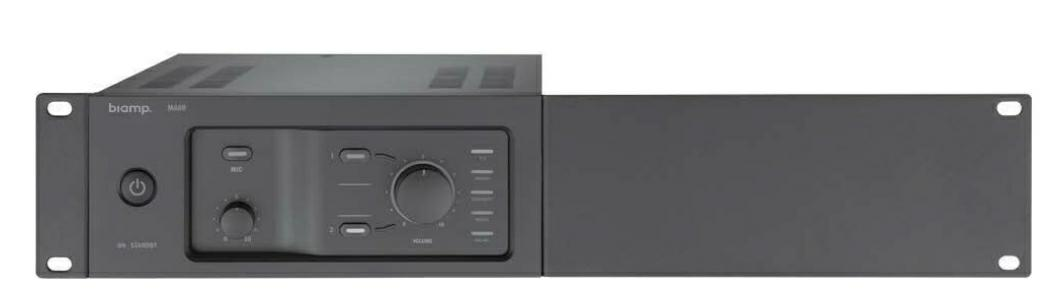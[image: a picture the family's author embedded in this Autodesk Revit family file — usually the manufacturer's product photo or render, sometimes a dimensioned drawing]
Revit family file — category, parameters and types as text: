
# Revit family: 1Electronics_Amplifier_Biamp_Commercial-Audio-Mixing-Amplifiers_MA30_MA60
name_source: partatom
category: Communication Devices
units: mm (PartAtom-declared; Revit-internal decimal feet)

## family parameters
Cut with Voids When Loaded = No
Host = Face
Maintain Annotation Orientation = No
OmniClass Number = 23.85.10.11.14
OmniClass Title = Audio Equipment
Part Type = Normal
Room Calculation Point = No
Round Connector Dimension = Use Diameter
Shared = No

## types (2) — shared parameters
Altitude = 0-6,600 ft (0-2000m) MSL
Compliance = FCC Part 15B (USA) UL listed (USA and Canada) CE Marked (Europe) RoHS Directive (Europe)
Cooling = Convection
Default Elevation = 4' - 0"
Depth = 0' - 10"
Dynamic Power = 35 W
Front Panel Indicators = Signal present, clipping, overload condition, emergency mode active, paging active, VOX active
Height = 0' - 3 1/2"
Housing Material = Biamp - Metal - Black
Humidity = 0-95% relative humidity (non-condensing)
Inputs 1-2 = -44 dBV (6 mVrms ± 10%)
Low Impedance Mode = Yes
Manufacturer = Biamp
Mic (Balanced, VOX of) = -70 dBV (0.3 mVrms ± 10%)
Mic (RCA) = -46 dBV (5 mVrms ± 10%)
Minimum Operational Load = 4Ω
No mount = No mount
Number of Output Channels = 1
Number of Poles = 1
Output Connectors = 4-pin, 0.3 inch (7.6 mm) Euroblock
Power Factor = 1
Product Documentation Link = https://downloads.biamp.com
Product Page URL = https://www.biamp.com
Product data url = https://www.bimobject.com
Protection = Temperature, overcurrent,overvoltage, undervoltage
RMK-1 = RMK-1
RMK-2 = RMK-2
RMS Output Power (1% THD) = 30 W
SNR (1% THD) = > 90 dB
THD+N (@ -6dB) = < 0.5%
Temperature Range = 32 - 95° F (0 – 35° C)
Time to Auto Standby = 10 min
Topology = Class D
URL = https://www.biamp.com
UTMK-1 = UTMK-1
Voltage = 120 V
Weight = 5.29 lb
Width = 0' - 8 1/2"

## per-type parameters (varying)
| type | Apparent Load | Connector Description | Description | Max Power Consumption |
| MA30 | 60 VA | 100-240V/50-60Hz/60W | MA30 30W Mixing Amplifier | 60 W |
| MA60 | 100 VA | 100-240V/50-60Hz/100W | MA60 60W Mixing Amplifier | 100 W |

note: column(s) folded — value = type name in every type: Model

## geometry (parser evidence)
native form markers: Sweep x13
no freeform markers — native parametric forms only
